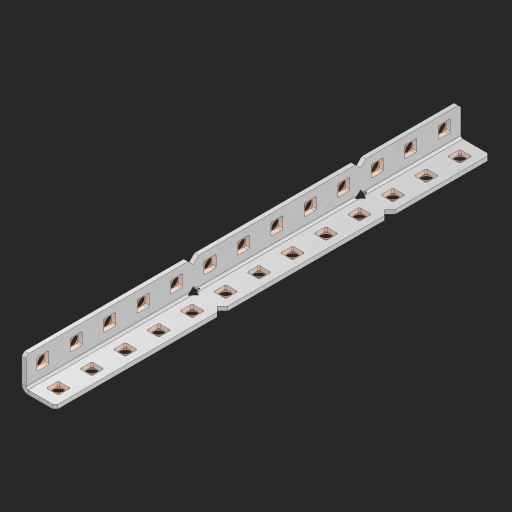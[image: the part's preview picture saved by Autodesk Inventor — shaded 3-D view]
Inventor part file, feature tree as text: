
AUTODESK INVENTOR PART (.ipt)
format: ipt  version: 2023 (Build 270158000, 158)  size: 664,576 bytes
history: native  units: in
note: dims shown in document units (in); Inventor stores cm internally (conversion verified against a paired STEP export)
features: other x32, extrude x27, sheet_metal_op x8, sketch x5, pattern_linear x1, mirror x1, chamfer x1
ambient origin geometry x8: Origin, YZ Plane, XZ Plane, XY Plane, X Axis, Y Axis, Z Axis, Center Point
bodies: Solid1 (feature_tree), Body (feature_tree)
feature tree (75):
  sheet_metal_op  "Flanges"
  sheet_metal_op  "Body Pattern"
  other  "Arc Length"
  pattern_linear  "Notch Pattern"  Spacing1=0.125in  [1 undecoded]
  other  "Diagonal Plane"
  mirror  "Everything Mirrored"
  chamfer  "End Chamfer"
  sketch  "Sketch1"  dims[d0=0.5in]
  other  "Plate1"
  sketch  "Sketch2"  dims[d1=6.5in]
  other  "Plate2"
  sheet_metal_op  "Bend1"
  sheet_metal_op  "Corner1"
  sketch  "Sketch8"  dims[d2=0.0625in]
  sketch  "Sketch9"  dims[d3=0.0625in]
  other  "Srf91"
  sheet_metal_op  "Body Pattern Sketch"
  other  "Srf92"
  sketch  "Sketch13"  dims[d4=0.0312in d5=0.125in d6=0.0625in d7=0.5in d8=90.0deg d9=0.0312in d10=0.25in d11=0.0625in d12=0.0625in d49=0.182in d50=0.02in d52=0.25in d53=0.0625in d54=0.0in d55=0.172in d56=1.0in d57=0.0in d85=0.1473in d86=0.1782in d89=0.0625in d90=0.0in d91=0.04in d92=0.0491in d95=2.5in d96=0.04in d97=0.25in d98=45.0deg d123=0.204in d126=0.0491in d127=0.1473in d128=0.08in d129=0.04in d130=2.5in d131=5.1181in d133=0.5in d134=0.3937in d136=1.0in]
  other  "Srf856"
  other  "Srf857"
  other  "Srf858"
  other  "Srf859"
  other  "Srf860"
  other  "Srf861"
  other  "Srf1275"
  other  "Srf1276"
  other  "Srf1278"
  other  "Srf1279"
  other  "Srf1280"
  other  "Srf1281"
  other  "Srf1282"
  other  "Srf1283"
  other  "Srf1383"
  other  "Srf1384"
  other  "Srf1385"
  other  "Srf1386"
  other  "Srf1387"
  other  "Srf1388"
  other  "Srf1475"
  other  "Srf1476"
  other  "Srf1477"
  other  "Srf1478"
  other  "Srf1479"
  other  "Srf1480"
  sheet_metal_op  "Body Stamp"
  sheet_metal_op  "Body Circle"
  sheet_metal_op  "Notch"
  extrude  "ExtrusionSrf92"  Depth=0.0625in
  extrude  "ExtrusionSrf856"  Depth=0.5in TaperAngle=90.0deg
  extrude  "ExtrusionSrf857"  Depth=0.25in
  extrude  "ExtrusionSrf858"  Depth=0.0625in
  extrude  "ExtrusionSrf859"  Depth=0.0625in
  extrude  "ExtrusionSrf860"  Depth=0.3937in
  extrude  "ExtrusionSrf861"  Depth=0.02in
  extrude  "ExtrusionSrf1275"  Depth=0.25in
  extrude  "ExtrusionSrf1276"  Depth=0.0625in
  extrude  "ExtrusionSrf1277"  TaperAngle=0.0deg  [1 undecoded]
  extrude  "ExtrusionSrf1278"  Depth=0.3937in
  extrude  "ExtrusionSrf1279"  Depth=0.3937in TaperAngle=0.0deg
  extrude  "ExtrusionSrf1280"  Depth=0.3937in
  extrude  "ExtrusionSrf1281"  Depth=0.3937in
  extrude  "ExtrusionSrf1282"  Depth=0.0625in
  extrude  "ExtrusionSrf1383"  Depth=0.3937in TaperAngle=0.0deg
  extrude  "ExtrusionSrf1384"  Depth=0.3937in
  extrude  "ExtrusionSrf1385"  Depth=0.25in TaperAngle=45.0deg
  extrude  "ExtrusionSrf1386"  Depth=0.3937in
  extrude  "ExtrusionSrf1387"  Depth=0.3937in
  extrude  "ExtrusionSrf1388"  Depth=0.3937in
  extrude  "ExtrusionSrf1475"  Depth=0.3937in
  extrude  "ExtrusionSrf1476"  Depth=0.3937in
  extrude  "ExtrusionSrf1477"  Depth=0.3937in
  extrude  "ExtrusionSrf1478"  Depth=0.3937in
  extrude  "ExtrusionSrf1479"  Depth=0.5in
  extrude  "ExtrusionSrf1480"  [1 undecoded]
note: 3 required parameter values undecoded (feature->parameter linkage not recoverable at this tier; creation-order binding heuristic only, values carry confidence <= 0.55)
